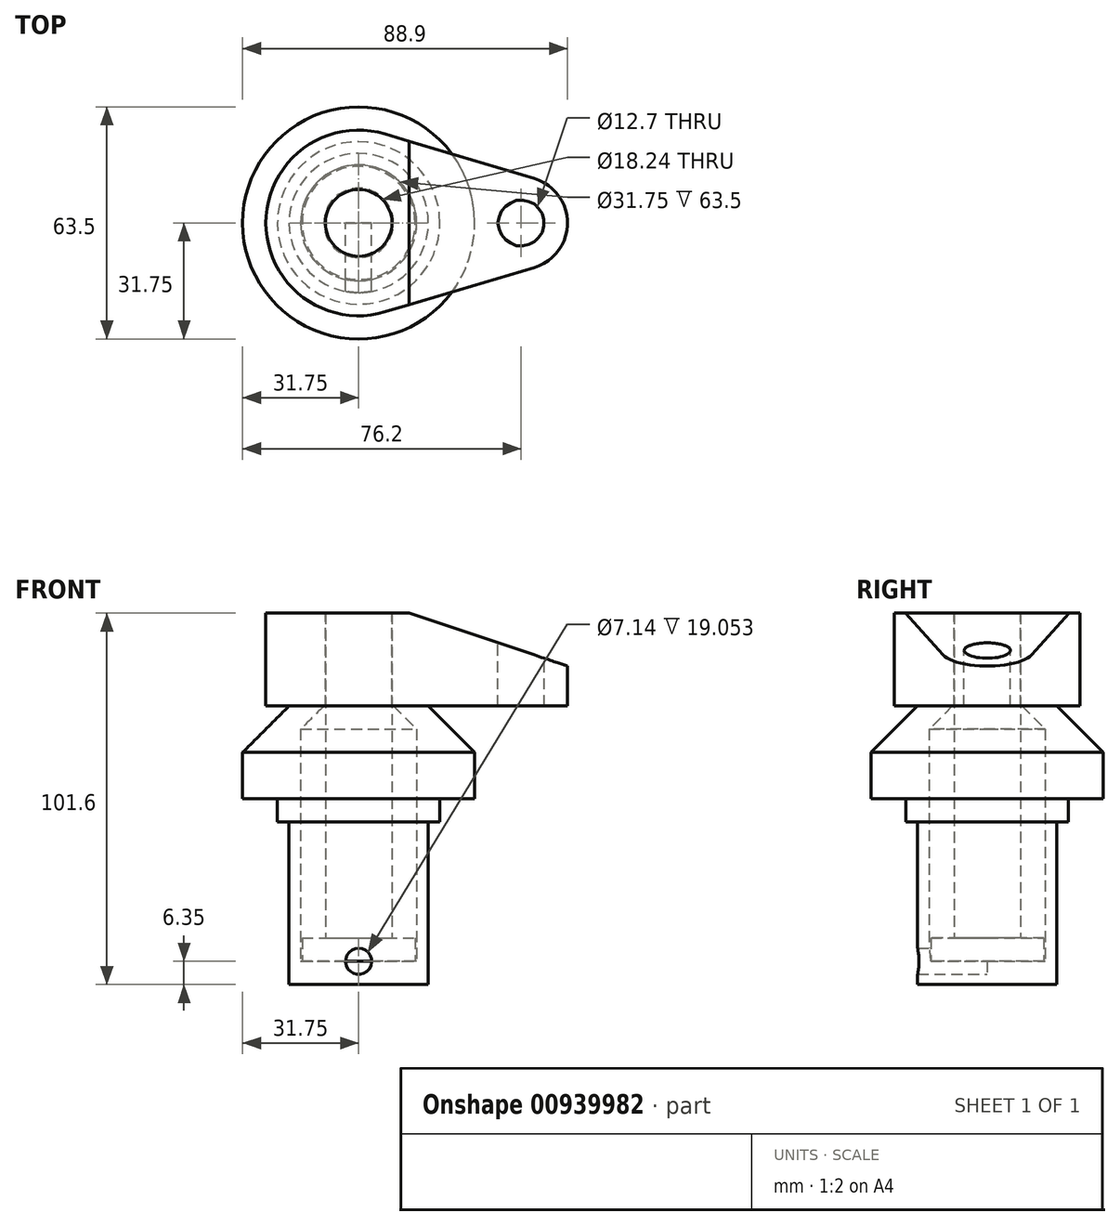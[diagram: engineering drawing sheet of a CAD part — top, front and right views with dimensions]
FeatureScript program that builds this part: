
annotation { "Feature Type Name" : "Feature", "Feature Type Description" : "" }
export const myFeature = defineFeature(function(context is Context, id is Id, definition is map)
    precondition{}
    {
        {
            var Q0;
            Q0=qCreatedBy(makeId("Front.planeOp"),FACE);
            var sketch = newSketch(context, id + "F0", { "sketchPlane" : qUnion([Q0])});
            skLineSegment(sketch, "E0", {"start": v(0, 0) * mm, "end": v(0, 38.1) * mm});
            skLineSegment(sketch, "E1", {"start": v(0, 38.1) * mm, "end": v(19.05, 38.1) * mm});
            skLineSegment(sketch, "E2", {"start": v(19.05, 38.1) * mm, "end": v(31.75, 25.4) * mm});
            skLineSegment(sketch, "E3", {"start": v(31.75, 25.4) * mm, "end": v(31.75, 12.7) * mm});
            skLineSegment(sketch, "E4", {"start": v(31.75, 12.7) * mm, "end": v(22.23, 12.7) * mm});
            skLineSegment(sketch, "E5", {"start": v(22.23, 12.7) * mm, "end": v(22.23, 6.35) * mm});
            skLineSegment(sketch, "E6", {"start": v(22.23, 6.35) * mm, "end": v(19.05, 6.35) * mm});
            skLineSegment(sketch, "E7", {"start": v(19.05, 6.35) * mm, "end": v(19.05, -38.1) * mm});
            skLineSegment(sketch, "E8", {"start": v(19.05, -38.1) * mm, "end": v(0, -38.1) * mm});
            skLineSegment(sketch, "E9", {"start": v(0, -38.1) * mm, "end": v(0, 0) * mm});
            skLineSegment(sketch, "E10", {"start": v(9.53, 38.1) * mm, "end": v(15.88, 31.75) * mm});
            skLineSegment(sketch, "E11", {"start": v(15.88, 31.75) * mm, "end": v(15.88, -31.75) * mm});
            skLineSegment(sketch, "E12", {"start": v(15.88, -31.75) * mm, "end": v(0, -31.75) * mm});
            skLineSegment(sketch, "E13", {"start": v(0, 38.1) * mm, "end": v(0, 45.6) * mm, "construction": true});
            skLineSegment(sketch, "E14", {"start": v(0, 63.5) * mm, "end": v(9.12, 63.5) * mm});
            skLineSegment(sketch, "E15", {"start": v(9.12, 63.5) * mm, "end": v(9.12, -25.4) * mm});
            skLineSegment(sketch, "E16", {"start": v(9.12, -25.4) * mm, "end": v(15.47, -25.4) * mm});
            skLineSegment(sketch, "E17", {"start": v(15.47, -31.75) * mm, "end": v(0, -31.75) * mm});
            skLineSegment(sketch, "E18", {"start": v(15.47, -25.4) * mm, "end": v(15.47, -31.75) * mm});
            skLineSegment(sketch, "E19", {"start": v(0, -31.75) * mm, "end": v(0, 63.5) * mm});
            skSolve(sketch);
        }
        {
            var Q0;
            {var subQ4=sQuery(id+"F0.wireOp",EDGE,"E2");Q0=makeQuery(id+"F0.imprint","IMPRINT",FACE,{"disambiguationData":[TD([[makeQuery(id+"F0.imprint","IMPRINT",EDGE,{"derivedFrom":subQ4}),-1.0]])]});}
            var Q1;
            Q1=sQuery(id+"F0.wireOp",EDGE,"E0");
            revolve(context, id + "F1", {"surfaceOperationType" : NewSurfaceOperationType.NEW, "entities" : qUnion([Q0]), "axis" : qUnion([Q1]), "revolveType" : RevolveType.FULL});
        }
        {
            var Q0;
            {var subQ5=sQuery(id+"F0.wireOp",EDGE,"E14");Q0=makeQuery(id+"F0.imprint","IMPRINT",FACE,{"disambiguationData":[TD([[makeQuery(id+"F0.imprint","IMPRINT",EDGE,{"derivedFrom":subQ5}),-1.0]])]});}
            var Q1;
            {var subQ1=sQuery(id+"F0.wireOp",EDGE,"E16");Q1=makeQuery(id+"F0.imprint","IMPRINT",FACE,{"disambiguationData":[TD([[makeQuery(id+"F0.imprint","IMPRINT",EDGE,{"derivedFrom":subQ1}),-1.0]])]});}
            var Q2;
            Q2=sQuery(id+"F0.wireOp",EDGE,"E19");
            revolve(context, id + "F2", {"surfaceOperationType" : NewSurfaceOperationType.NEW, "entities" : qUnion([Q0, Q1]), "axis" : qUnion([Q2]), "revolveType" : RevolveType.FULL});
        }
        {
            var Q0;
            Q0=makeQuery(id+"F2.opRevolve","SWEPT_FACE",FACE,{"disambiguationData":[OSD([sQuery(id+"F0.wireOp",EDGE,"E14")])]});
            var sketch = newSketch(context, id + "F3", { "sketchPlane" : qUnion([Q0])});
            skCircle(sketch, "E20", {"center": v(0, 0) * mm, "radius": 25.4 * mm});
            skCircle(sketch, "E21", {"center": v(44.45, 0) * mm, "radius": 6.35 * mm});
            skLineSegment(sketch, "E22", {"start": v(44.45, 0) * mm, "end": v(0, 0) * mm, "construction": true});
            skCircle(sketch, "E23", {"center": v(44.45, 0) * mm, "radius": 12.7 * mm});
            skLineSegment(sketch, "E24", {"start": v(7.26, 24.34) * mm, "end": v(48.08, 12.17) * mm});
            skLineSegment(sketch, "E25", {"start": v(48.08, -12.17) * mm, "end": v(7.26, -24.34) * mm});
            skCircle(sketch, "E26.0", {"center": v(0, 0) * mm, "radius": 9.12 * mm});
            skSolve(sketch);
        }
        {
            var Q0;
            Q0=makeQuery(id+"F3.imprint","IMPRINT",FACE,{"disambiguationData":[TD([[makeQuery(id+"F3.imprint","IMPRINT",EDGE,{"derivedFrom":sQuery(id+"F3.wireOp",EDGE,"E26.0")}),1.0]])]});
            var Q1;
            {var subQ0=sQuery(id+"F3.wireOp",EDGE,"E24");Q1=makeQuery(id+"F3.imprint","IMPRINT",FACE,{"disambiguationData":[TD([[makeQuery(id+"F3.imprint","IMPRINT",EDGE,{"derivedFrom":subQ0}),-1.0]])]});}
            var Q2;
            Q2=makeQuery(id+"F3.imprint","IMPRINT",FACE,{"disambiguationData":[TD([[makeQuery(id+"F3.imprint","IMPRINT",EDGE,{"derivedFrom":sQuery(id+"F3.wireOp",EDGE,"E21")}),-1.0]])]});
            var Q3;
            Q3=makeQuery(id+"F1.opRevolve","SWEPT_FACE",FACE,{"disambiguationData":[OSD([sQuery(id+"F0.wireOp",EDGE,"E1")])]});
            extrude(context, id + "F4", {"entities" : qUnion([Q0, Q1, Q2]), "endBound" : BoundingType.UP_TO_SURFACE, "oppositeDirection" : true, "depth" : 25.4 * mm, "endBoundEntityFace" : qUnion([Q3]), "offsetDistance" : 25.4 * mm});
        }
        {
            var Q0;
            Q0=qCreatedBy(makeId("Front.planeOp"),FACE);
            var sketch = newSketch(context, id + "F5", { "sketchPlane" : qUnion([Q0])});
            skLineSegment(sketch, "E27.0.0", {"start": v(48.08, 63.5) * mm, "end": v(48.08, 38.1) * mm, "construction": true});
            skLineSegment(sketch, "E27.0.1", {"start": v(48.08, 38.1) * mm, "end": v(57.15, 38.1) * mm, "construction": true});
            skLineSegment(sketch, "E27.0.2", {"start": v(48.08, 38.1) * mm, "end": v(48.08, 63.5) * mm, "construction": true});
            skLineSegment(sketch, "E27.0.3", {"start": v(48.08, 63.5) * mm, "end": v(57.15, 63.5) * mm, "construction": true});
            skLineSegment(sketch, "E28", {"start": v(57.15, 63.5) * mm, "end": v(57.15, 49.04) * mm});
            skLineSegment(sketch, "E29", {"start": v(57.15, 49.04) * mm, "end": v(13.8, 63.5) * mm});
            skLineSegment(sketch, "E30", {"start": v(13.8, 63.5) * mm, "end": v(57.15, 63.5) * mm});
            skSolve(sketch);
        }
        {
            var Q0;
            Q0=makeQuery(id+"F5.imprint","IMPRINT",FACE,{"disambiguationData":[TD([[makeQuery(id+"F5.imprint","IMPRINT",EDGE,{"derivedFrom":sQuery(id+"F5.wireOp",EDGE,"E28")}),-1.0]])]});
            extrude(context, id + "F6", {"entities" : qUnion([Q0]), "operationType" : NewBodyOperationType.REMOVE, "endBound" : BoundingType.THROUGH_ALL, "oppositeDirection" : true, "depth" : 25.4 * mm, "offsetDistance" : 25.4 * mm, "hasSecondDirection" : true, "secondDirectionBound" : SecondDirectionBoundingType.THROUGH_ALL, "secondDirectionOppositeDirection" : false, "secondDirectionDepth" : 25.4 * mm});
        }
        {
            var Q0;
            Q0=qCreatedBy(makeId("Front.planeOp"),FACE);
            var sketch = newSketch(context, id + "F7", { "sketchPlane" : qUnion([Q0])});
            skPoint(sketch, "E31", {"position": v(0, -31.75) * mm});
            skLineSegment(sketch, "E32", {"start": v(0, -31.75) * mm, "end": v(0, -38.1) * mm, "construction": true});
            skLineSegment(sketch, "E33.0.0", {"start": v(19.05, -38.1) * mm, "end": v(-19.05, -38.1) * mm, "construction": true});
            skSolve(sketch);
        }
        {
            var Q0;
            Q0=sQuery(id+"F7.wireOp",VERTEX,"E31");
            var Q1;
            Q1=makeQuery(id+"F1.opRevolve","SWEPT_BODY",BODY,{"disambiguationData":[OSD([sQuery(id+"F0.wireOp",EDGE,"E1"),sQuery(id+"F0.wireOp",EDGE,"E2"),sQuery(id+"F0.wireOp",EDGE,"E3"),sQuery(id+"F0.wireOp",EDGE,"E4"),sQuery(id+"F0.wireOp",EDGE,"E5"),sQuery(id+"F0.wireOp",EDGE,"E6"),sQuery(id+"F0.wireOp",EDGE,"E7"),sQuery(id+"F0.wireOp",EDGE,"E8"),sQuery(id+"F0.wireOp",EDGE,"E9"),sQuery(id+"F0.wireOp",EDGE,"E10"),sQuery(id+"F0.wireOp",EDGE,"E11"),sQuery(id+"F0.wireOp",EDGE,"E12"),sQuery(id+"F0.wireOp",EDGE,"E17")])]});
            hole(context, id + "F8", {"style" : HoleStyle.SIMPLE, "endStyle" : HoleEndStyle.THROUGH, "oppositeDirection" : true, "standardTappedOrClearance" : lookupTablePath({ "fit" : "Normal (ASME)", "standard" : "ANSI", "size" : "1/4", "type" : "Clearance" }), "standardBlindInLast" : lookupTablePath({ "fit" : "Normal", "standard" : "ANSI", "engagement" : "75%", "pitch" : "20 tpi", "size" : "1/4", "type" : "Clearance & tapped" }), "holeDiameter" : 7.14 * mm, "majorDiameter" : 6.35 * mm, "isTappedThrough" : true, "tappedDepth" : 12.7 * mm, "tapClearance" : 3, "locations" : qUnion([Q0]), "scope" : qUnion([Q1])});
        }
    });
